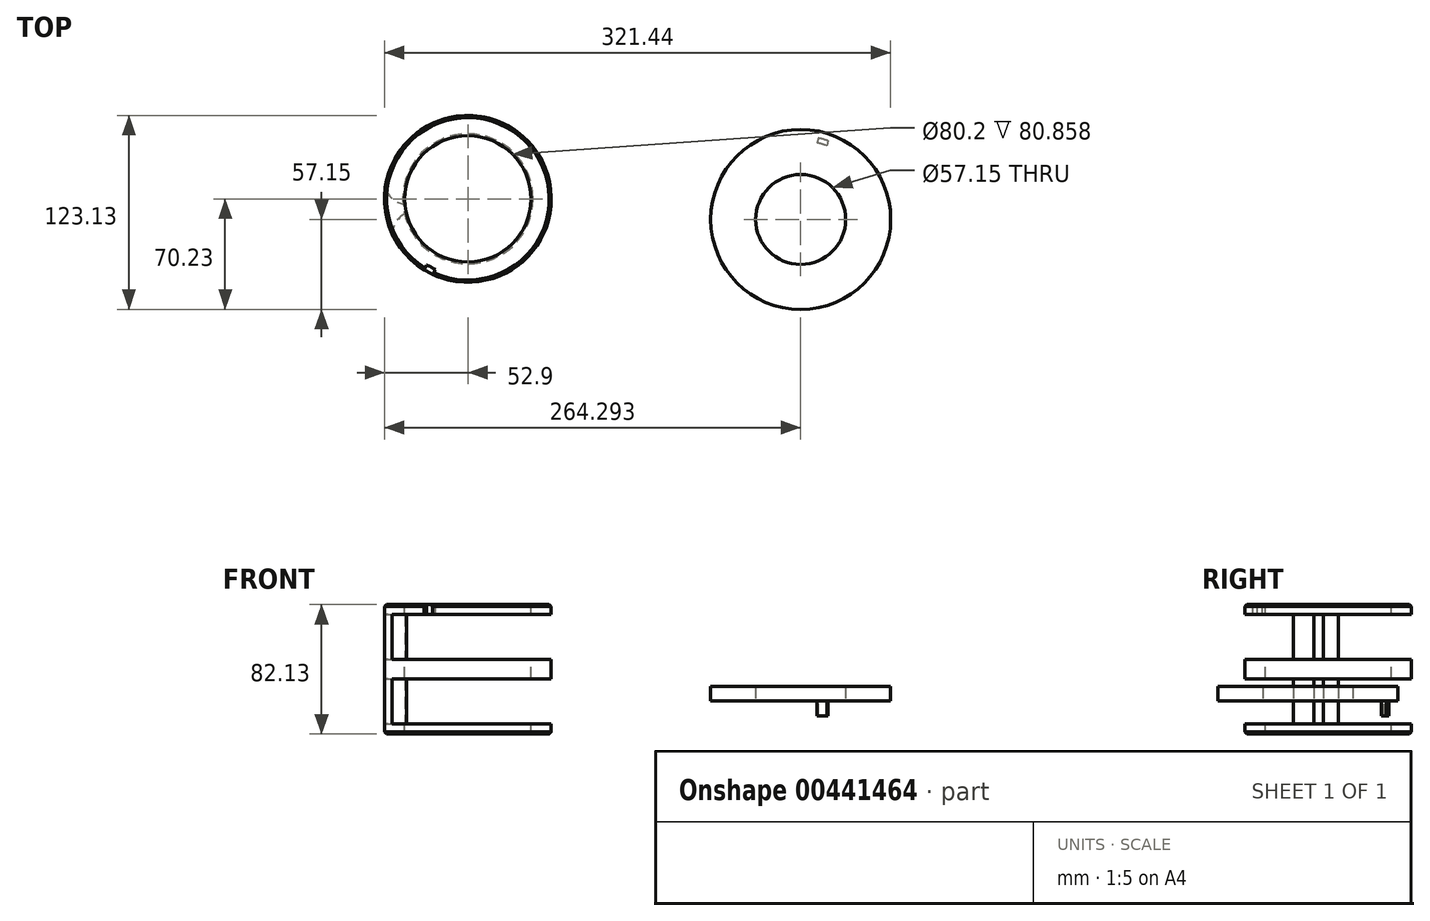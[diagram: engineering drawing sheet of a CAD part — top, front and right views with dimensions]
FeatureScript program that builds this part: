
annotation { "Feature Type Name" : "Feature", "Feature Type Description" : "" }
export const myFeature = defineFeature(function(context is Context, id is Id, definition is map)
    precondition{}
    {
        {
            var Q0;
            Q0=qCreatedBy(makeId("Front.planeOp"),FACE);
            var sketch = newSketch(context, id + "F0", { "sketchPlane" : qUnion([Q0])});
            skLineSegment(sketch, "E0", {"start": v(0, 92.26) * mm, "end": v(0, -92.26) * mm, "construction": true});
            skLineSegment(sketch, "E1.bottom", {"start": v(40.1, 61.04) * mm, "end": v(52.9, 61.04) * mm});
            skLineSegment(sketch, "E1.top", {"start": v(40.1, 54.69) * mm, "end": v(52.9, 54.69) * mm});
            skLineSegment(sketch, "E1.left", {"start": v(40.1, 61.04) * mm, "end": v(40.1, 54.69) * mm});
            skLineSegment(sketch, "E1.right", {"start": v(52.9, 61.04) * mm, "end": v(52.9, 54.69) * mm});
            skLineSegment(sketch, "E2.bottom", {"start": v(40.1, 26.11) * mm, "end": v(52.9, 26.11) * mm});
            skLineSegment(sketch, "E2.top", {"start": v(40.1, 13.91) * mm, "end": v(52.9, 13.91) * mm});
            skLineSegment(sketch, "E2.left", {"start": v(40.1, 26.11) * mm, "end": v(40.1, 13.91) * mm});
            skLineSegment(sketch, "E2.right", {"start": v(52.9, 26.11) * mm, "end": v(52.9, 13.91) * mm});
            skLineSegment(sketch, "E3.bottom", {"start": v(40.1, -14.66) * mm, "end": v(52.9, -14.66) * mm});
            skLineSegment(sketch, "E3.top", {"start": v(40.1, -21.09) * mm, "end": v(52.9, -21.09) * mm});
            skLineSegment(sketch, "E3.left", {"start": v(40.1, -14.66) * mm, "end": v(40.1, -21.09) * mm});
            skLineSegment(sketch, "E3.right", {"start": v(52.9, -14.66) * mm, "end": v(52.9, -21.09) * mm});
            skSolve(sketch);
        }
        {
            var Q0;
            Q0=makeQuery(id+"F0.imprint","IMPRINT",FACE,{"disambiguationData":[TD([[makeQuery(id+"F0.imprint","IMPRINT",EDGE,{"derivedFrom":sQuery(id+"F0.wireOp",EDGE,"E1.bottom")}),-1.0]])]});
            var Q1;
            Q1=makeQuery(id+"F0.imprint","IMPRINT",FACE,{"disambiguationData":[TD([[makeQuery(id+"F0.imprint","IMPRINT",EDGE,{"derivedFrom":sQuery(id+"F0.wireOp",EDGE,"E2.bottom")}),-1.0]])]});
            var Q2;
            Q2=makeQuery(id+"F0.imprint","IMPRINT",FACE,{"disambiguationData":[TD([[makeQuery(id+"F0.imprint","IMPRINT",EDGE,{"derivedFrom":sQuery(id+"F0.wireOp",EDGE,"E3.bottom")}),-1.0]])]});
            var Q3;
            Q3=sQuery(id+"F0.wireOp",EDGE,"E0");
            revolve(context, id + "F1", {"entities" : qUnion([Q0, Q1, Q2]), "axis" : qUnion([Q3]), "revolveType" : RevolveType.FULL});
        }
        {
            var Q0;
            Q0=makeQuery(id+"F1.opRevolve","SWEPT_FACE",FACE,{"disambiguationData":[OSD([sQuery(id+"F0.wireOp",EDGE,"E3.bottom")])]});
            var sketch = newSketch(context, id + "F2", { "sketchPlane" : qUnion([Q0])});
            skPoint(sketch, "E4", {"position": v(-39.07, -9.02) * mm});
            skPoint(sketch, "E5", {"position": v(-39.97, -3.26) * mm});
            skPoint(sketch, "E6", {"position": v(-48, -22.22) * mm});
            skPoint(sketch, "E7", {"position": v(-52.52, 6.38) * mm});
            skArc(sketch, "E8", {"start": v(-39.07, -9.02) * mm, "mid": v(-45.44, -14.33) * mm, "end": v(-48, -22.22) * mm});
            skArc(sketch, "E9", {"start": v(-52.52, 6.38) * mm, "mid": v(-47.61, -0.23) * mm, "end": v(-39.97, -3.26) * mm});
            skCircle(sketch, "E10.0", {"center": v(0, 0) * mm, "radius": 52.9 * mm});
            skCircle(sketch, "E11.0", {"center": v(0, 0) * mm, "radius": 40.1 * mm});
            skSolve(sketch);
        }
        {
            var Q0;
            {var subQ0=sQuery(id+"F2.wireOp",EDGE,"E8");Q0=makeQuery(id+"F2.imprint","IMPRINT",FACE,{"disambiguationData":[TD([[makeQuery(id+"F2.imprint","IMPRINT",EDGE,{"derivedFrom":subQ0}),-1.0]])]});}
            extrude(context, id + "F3", {"entities" : qUnion([Q0]), "operationType" : NewBodyOperationType.ADD, "depth" : 70.6 * mm});
        }
        {
            var Q0;
            Q0=makeQuery(id+"F1.opRevolve","SWEPT_EDGE",EDGE,{"disambiguationData":[OSD([sQuery(id+"F0.wireOp",EDGE,"E3.top"),sQuery(id+"F0.wireOp",EDGE,"E3.right")])]});
            var Q1;
            Q1=makeQuery(id+"F1.opRevolve","SWEPT_EDGE",EDGE,{"disambiguationData":[OSD([sQuery(id+"F0.wireOp",EDGE,"E1.bottom"),sQuery(id+"F0.wireOp",EDGE,"E1.right")])]});
            var Q2;
            Q2=makeQuery(id+"F1.opRevolve","SWEPT_EDGE",EDGE,{"disambiguationData":[OSD([sQuery(id+"F0.wireOp",EDGE,"E3.top"),sQuery(id+"F0.wireOp",EDGE,"E3.left")])]});
            chamfer(context, id + "F4", {"entities" : qUnion([Q0, Q1, Q2]), "width" : 1.27 * mm, "tangentPropagation" : true});
        }
        {
            var Q0;
            Q0=makeQuery(id+"F1.opRevolve","SWEPT_FACE",FACE,{"disambiguationData":[OSD([sQuery(id+"F0.wireOp",EDGE,"E1.bottom")])]});
            var sketch = newSketch(context, id + "F5", { "sketchPlane" : qUnion([Q0])});
            skLineSegment(sketch, "E12", {"start": v(-22.52, -48.26) * mm, "end": v(-20.67, -44.93) * mm});
            skLineSegment(sketch, "E13", {"start": v(-28.03, -45.14) * mm, "end": v(-26.27, -41.9) * mm});
            skArc(sketch, "E14", {"start": v(-20.67, -44.93) * mm, "mid": v(-23.42, -43.32) * mm, "end": v(-26.27, -41.9) * mm});
            skArc(sketch, "E15", {"start": v(-22.52, -48.26) * mm, "mid": v(-25.23, -46.63) * mm, "end": v(-28.03, -45.14) * mm});
            skSolve(sketch);
        }
        {
            var Q0;
            {var subQ0=sQuery(id+"F5.wireOp",EDGE,"E14");Q0=makeQuery(id+"F5.imprint","IMPRINT",FACE,{"disambiguationData":[TD([[makeQuery(id+"F5.imprint","IMPRINT",EDGE,{"derivedFrom":subQ0}),1.0]])]});}
            var Q1;
            {var subQ0=sQuery(id+"F5.wireOp",EDGE,"E15");Q1=makeQuery(id+"F5.imprint","IMPRINT",FACE,{"disambiguationData":[TD([[makeQuery(id+"F5.imprint","IMPRINT",EDGE,{"derivedFrom":subQ0}),-1.0]])]});}
            extrude(context, id + "F6", {"entities" : qUnion([Q0, Q1]), "operationType" : NewBodyOperationType.REMOVE, "oppositeDirection" : true, "depth" : 6.35 * mm});
        }
        {
            var Q0;
            Q0=qCreatedBy(makeId("Top.planeOp"),FACE);
            var sketch = newSketch(context, id + "F7", { "sketchPlane" : qUnion([Q0])});
            skCircle(sketch, "E16", {"center": v(211.4, -13.08) * mm, "radius": 57.15 * mm});
            skCircle(sketch, "E17", {"center": v(211.4, -13.08) * mm, "radius": 28.58 * mm});
            skSolve(sketch);
        }
        {
            var Q0;
            Q0=makeQuery(id+"F7.imprint","IMPRINT",FACE,{"disambiguationData":[TD([[makeQuery(id+"F7.imprint","IMPRINT",EDGE,{"derivedFrom":sQuery(id+"F7.wireOp",EDGE,"E16")}),1.0]])]});
            extrude(context, id + "F8", {"entities" : qUnion([Q0]), "depth" : 8.96 * mm});
        }
        {
            var Q0;
            Q0=makeQuery(id+"F8.opExtrude","CAP_FACE",FACE,{"disambiguationData":[OSD([sQuery(id+"F7.wireOp",EDGE,"E16"),sQuery(id+"F7.wireOp",EDGE,"E17")])],"isStart":true});
            var sketch = newSketch(context, id + "F9", { "sketchPlane" : qUnion([Q0])});
            skPoint(sketch, "E18", {"position": v(228.8, -36.88) * mm});
            skPoint(sketch, "E19", {"position": v(222.68, -38.6) * mm});
            skLineSegment(sketch, "E20", {"start": v(228.8, -36.88) * mm, "end": v(227.99, -33.8) * mm});
            skLineSegment(sketch, "E21", {"start": v(222.68, -38.6) * mm, "end": v(221.78, -35.55) * mm});
            skArc(sketch, "E22", {"start": v(221.78, -35.55) * mm, "mid": v(224.91, -34.78) * mm, "end": v(227.99, -33.8) * mm});
            skArc(sketch, "E23", {"start": v(222.68, -38.6) * mm, "mid": v(225.76, -37.83) * mm, "end": v(228.8, -36.88) * mm});
            skSolve(sketch);
        }
        {
            var Q0;
            Q0=makeQuery(id+"F9.imprint","IMPRINT",FACE,{"disambiguationData":[TD([[makeQuery(id+"F9.imprint","IMPRINT",EDGE,{"derivedFrom":sQuery(id+"F9.wireOp",EDGE,"E20")}),1.0]])]});
            extrude(context, id + "F10", {"entities" : qUnion([Q0]), "operationType" : NewBodyOperationType.ADD, "depth" : 9.52 * mm});
        }
    });
